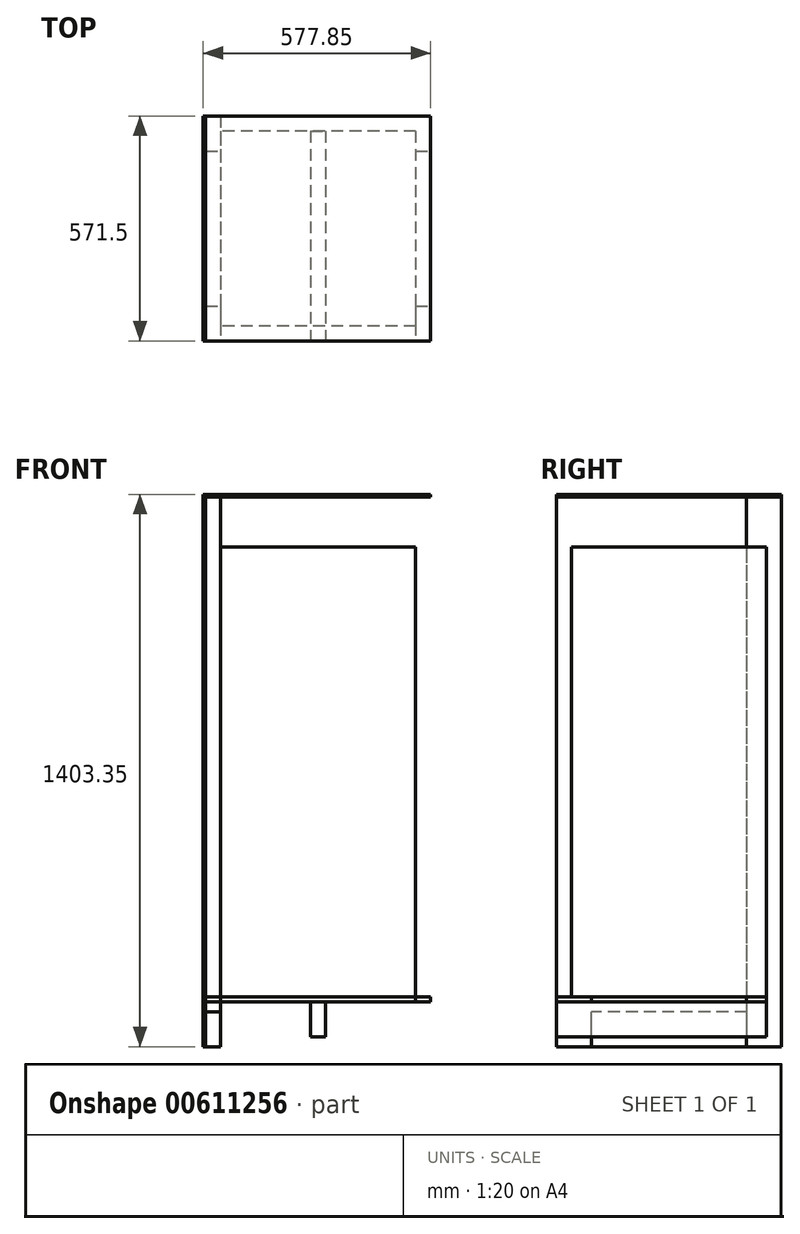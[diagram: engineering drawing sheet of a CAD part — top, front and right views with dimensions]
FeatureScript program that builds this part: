
annotation { "Feature Type Name" : "Feature", "Feature Type Description" : "" }
export const myFeature = defineFeature(function(context is Context, id is Id, definition is map)
    precondition{}
    {
        {
            var Q0;
            Q0=qCreatedBy(makeId("Top.planeOp"),FACE);
            var sketch = newSketch(context, id + "F0", { "sketchPlane" : qUnion([Q0])});
            skLineSegment(sketch, "E0.bottom", {"start": v(247.65, 247.65) * mm, "end": v(-247.65, 247.65) * mm});
            skLineSegment(sketch, "E0.top", {"start": v(247.65, -247.65) * mm, "end": v(-247.65, -247.65) * mm});
            skLineSegment(sketch, "E0.left", {"start": v(247.65, 247.65) * mm, "end": v(247.65, -247.65) * mm});
            skLineSegment(sketch, "E0.right", {"start": v(-247.65, 247.65) * mm, "end": v(-247.65, -247.65) * mm});
            skPoint(sketch, "E0.middle", {"position": v(0, 0) * mm});
            skSolve(sketch);
        }
        {
            var Q0;
            Q0 = qSketchRegion(id + "F0", true);
            extrude(context, id + "F1", {"entities" : qUnion([Q0]), "endBound" : BoundingType.SYMMETRIC, "depth" : 1143 * mm, "offsetDistance" : 25.4 * mm});
        }
        {
            var Q0;
            Q0=qCreatedBy(makeId("Top.planeOp"),FACE);
            var sketch = newSketch(context, id + "F2", { "sketchPlane" : qUnion([Q0])});
            skLineSegment(sketch, "E1.bottom", {"start": v(-247.65, 285.75) * mm, "end": v(-285.75, 285.75) * mm});
            skLineSegment(sketch, "E1.top", {"start": v(-247.65, 196.85) * mm, "end": v(-285.75, 196.85) * mm});
            skLineSegment(sketch, "E1.left", {"start": v(-247.65, 285.75) * mm, "end": v(-247.65, 196.85) * mm});
            skLineSegment(sketch, "E1.right", {"start": v(-285.75, 285.75) * mm, "end": v(-285.75, 196.85) * mm});
            skSolve(sketch);
        }
        {
            var Q0;
            Q0 = qSketchRegion(id + "F2", true);
            extrude(context, id + "F3", {"entities" : qUnion([Q0]), "endBound" : BoundingType.SYMMETRIC, "depth" : 1397 * mm, "offsetDistance" : 25.4 * mm});
        }
        {
            var Q0;
            Q0=makeQuery(id+"F1.opExtrude","CAP_FACE",FACE,{"disambiguationData":[OSD([sQuery(id+"F0.wireOp",EDGE,"E0.bottom"),sQuery(id+"F0.wireOp",EDGE,"E0.top"),sQuery(id+"F0.wireOp",EDGE,"E0.left"),sQuery(id+"F0.wireOp",EDGE,"E0.right")])],"isStart":true});
            var sketch = newSketch(context, id + "F4", { "sketchPlane" : qUnion([Q0])});
            skLineSegment(sketch, "E2.top", {"start": v(-247.65, 285.75) * mm, "end": v(247.65, 285.75) * mm});
            skLineSegment(sketch, "E2.left", {"start": v(-247.65, -247.65) * mm, "end": v(-247.65, -196.85) * mm});
            skLineSegment(sketch, "E2.right", {"start": v(247.65, -247.65) * mm, "end": v(247.65, -196.85) * mm});
            skLineSegment(sketch, "E3.bottom", {"start": v(-285.75, -196.85) * mm, "end": v(-247.65, -196.85) * mm});
            skLineSegment(sketch, "E3.top", {"start": v(-285.75, 196.85) * mm, "end": v(-247.65, 196.85) * mm});
            skLineSegment(sketch, "E3.left", {"start": v(-285.75, -196.85) * mm, "end": v(-285.75, 196.85) * mm});
            skLineSegment(sketch, "E3.right", {"start": v(285.75, -196.85) * mm, "end": v(285.75, 196.85) * mm});
            skLineSegment(sketch, "E4.trimOffspring", {"start": v(-247.65, 196.85) * mm, "end": v(-247.65, 285.75) * mm});
            skLineSegment(sketch, "E5.trimOffspring", {"start": v(247.65, 196.85) * mm, "end": v(285.75, 196.85) * mm});
            skLineSegment(sketch, "E6.trimOffspring", {"start": v(247.65, 196.85) * mm, "end": v(247.65, 285.75) * mm});
            skLineSegment(sketch, "E7.trimOffspring", {"start": v(247.65, -196.85) * mm, "end": v(285.75, -196.85) * mm});
            skLineSegment(sketch, "E8", {"start": v(247.65, -247.65) * mm, "end": v(-247.65, -247.65) * mm});
            skSolve(sketch);
        }
        {
            var Q0;
            Q0 = qSketchRegion(id + "F4", true);
            extrude(context, id + "F5", {"entities" : qUnion([Q0]), "depth" : 12.7 * mm, "offsetDistance" : 25.4 * mm});
        }
        {
            var Q0;
            Q0=makeQuery(id+"F3.opExtrude","SWEPT_FACE",FACE,{"disambiguationData":[OSD([sQuery(id+"F2.wireOp",EDGE,"E1.right")])]});
            var sketch = newSketch(context, id + "F6", { "sketchPlane" : qUnion([Q0])});
            skLineSegment(sketch, "E9.bottom", {"start": v(-196.85, -698.5) * mm, "end": v(196.85, -698.5) * mm});
            skLineSegment(sketch, "E9.top", {"start": v(-196.85, -609.6) * mm, "end": v(196.85, -609.6) * mm});
            skLineSegment(sketch, "E9.left", {"start": v(-196.85, -698.5) * mm, "end": v(-196.85, -609.6) * mm});
            skLineSegment(sketch, "E9.right", {"start": v(196.85, -698.5) * mm, "end": v(196.85, -609.6) * mm});
            skSolve(sketch);
        }
        {
            var Q0;
            Q0 = qSketchRegion(id + "F6", true);
            var Q1;
            Q1=makeQuery(id+"F3.opExtrude","SWEPT_FACE",FACE,{"disambiguationData":[OSD([sQuery(id+"F2.wireOp",EDGE,"E1.left")])]});
            extrude(context, id + "F7", {"entities" : qUnion([Q0]), "endBound" : BoundingType.UP_TO_SURFACE, "oppositeDirection" : true, "depth" : 25.4 * mm, "endBoundEntityFace" : qUnion([Q1]), "offsetDistance" : 25.4 * mm});
        }
        {
            var Q0;
            Q0=makeQuery(id+"F5.opExtrude","SWEPT_FACE",FACE,{"disambiguationData":[OSD([sQuery(id+"F4.wireOp",EDGE,"E2.top")])]});
            var sketch = newSketch(context, id + "F8", { "sketchPlane" : qUnion([Q0])});
            skLineSegment(sketch, "E10", {"start": v(0, 0) * mm, "end": v(0, -793.25) * mm, "construction": true});
            skLineSegment(sketch, "E11.bottom", {"start": v(19.05, -584.2) * mm, "end": v(-19.05, -584.2) * mm});
            skLineSegment(sketch, "E11.top", {"start": v(19.05, -673.1) * mm, "end": v(-19.05, -673.1) * mm});
            skLineSegment(sketch, "E11.left", {"start": v(19.05, -584.2) * mm, "end": v(19.05, -673.1) * mm});
            skLineSegment(sketch, "E11.right", {"start": v(-19.05, -584.2) * mm, "end": v(-19.05, -673.1) * mm});
            skSolve(sketch);
        }
        {
            var Q0;
            Q0 = qSketchRegion(id + "F8", true);
            var Q1;
            Q1=makeQuery(id+"F5.opExtrude","SWEPT_FACE",FACE,{"disambiguationData":[OSD([sQuery(id+"F4.wireOp",EDGE,"E8")])]});
            extrude(context, id + "F9", {"entities" : qUnion([Q0]), "endBound" : BoundingType.UP_TO_SURFACE, "oppositeDirection" : true, "depth" : 25.4 * mm, "endBoundEntityFace" : qUnion([Q1]), "offsetDistance" : 25.4 * mm});
        }
        {
            var Q0;
            Q0=makeQuery(id+"F3.opExtrude","CAP_FACE",FACE,{"disambiguationData":[OSD([sQuery(id+"F2.wireOp",EDGE,"E1.bottom"),sQuery(id+"F2.wireOp",EDGE,"E1.top"),sQuery(id+"F2.wireOp",EDGE,"E1.left"),sQuery(id+"F2.wireOp",EDGE,"E1.right")])],"isStart":false});
            var sketch = newSketch(context, id + "F10", { "sketchPlane" : qUnion([Q0])});
            skLineSegment(sketch, "E12.bottom", {"start": v(-285.75, 285.75) * mm, "end": v(285.75, 285.75) * mm});
            skLineSegment(sketch, "E12.top", {"start": v(-285.75, -285.75) * mm, "end": v(285.75, -285.75) * mm});
            skLineSegment(sketch, "E12.left", {"start": v(-285.75, 285.75) * mm, "end": v(-285.75, -285.75) * mm});
            skLineSegment(sketch, "E12.right", {"start": v(285.75, 285.75) * mm, "end": v(285.75, -285.75) * mm});
            skSolve(sketch);
        }
        {
            var Q0;
            Q0 = qSketchRegion(id + "F10", true);
            extrude(context, id + "F11", {"entities" : qUnion([Q0]), "depth" : 6.35 * mm, "offsetDistance" : 25.4 * mm});
        }
        {
            var Q0;
            Q0=makeQuery(id+"F3.opExtrude","SWEPT_FACE",FACE,{"disambiguationData":[OSD([sQuery(id+"F2.wireOp",EDGE,"E1.right")])]});
            var sketch = newSketch(context, id + "F12", { "sketchPlane" : qUnion([Q0])});
            skLineSegment(sketch, "E13.bottom", {"start": v(-285.75, -698.5) * mm, "end": v(285.75, -698.5) * mm});
            skLineSegment(sketch, "E13.top", {"start": v(-285.75, 704.85) * mm, "end": v(285.75, 704.85) * mm});
            skLineSegment(sketch, "E13.left", {"start": v(-285.75, -698.5) * mm, "end": v(-285.75, 704.85) * mm});
            skLineSegment(sketch, "E13.right", {"start": v(285.75, -698.5) * mm, "end": v(285.75, 704.85) * mm});
            skSolve(sketch);
        }
        {
            var Q0;
            Q0 = qSketchRegion(id + "F12", true);
            extrude(context, id + "F13", {"entities" : qUnion([Q0]), "depth" : 6.35 * mm, "offsetDistance" : 25.4 * mm});
        }
    });
